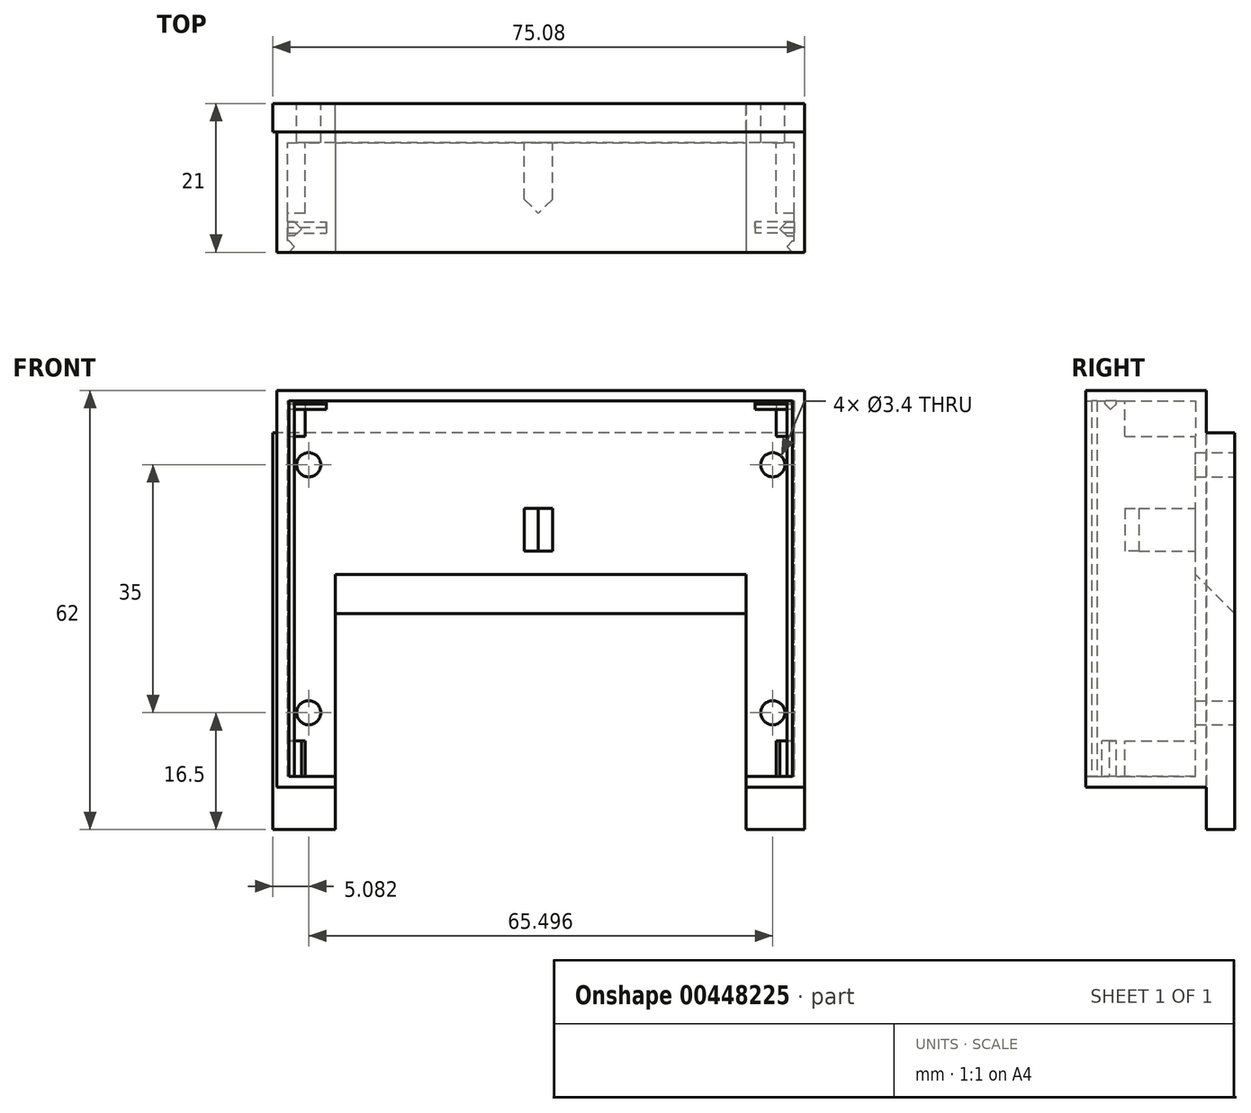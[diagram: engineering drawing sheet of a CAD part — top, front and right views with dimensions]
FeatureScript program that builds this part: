
annotation { "Feature Type Name" : "Feature", "Feature Type Description" : "" }
export const myFeature = defineFeature(function(context is Context, id is Id, definition is map)
    precondition{}
    {
        {
            var Q0;
            Q0=qCreatedBy(makeId("Front.planeOp"),FACE);
            var sketch = newSketch(context, id + "F0", { "sketchPlane" : qUnion([Q0])});
            skLineSegment(sketch, "E0.bottom", {"start": v(0, 0) * mm, "end": v(-74.5, 0) * mm});
            skLineSegment(sketch, "E0.top", {"start": v(0, 56) * mm, "end": v(-74.5, 56) * mm});
            skLineSegment(sketch, "E0.left", {"start": v(0, 0) * mm, "end": v(0, 56) * mm});
            skLineSegment(sketch, "E0.right", {"start": v(-74.5, 0) * mm, "end": v(-74.5, 56) * mm});
            skSolve(sketch);
        }
        {
            var Q0;
            Q0=makeQuery(id+"F0.imprint","IMPRINT",FACE,{"disambiguationData":[TD([[makeQuery(id+"F0.imprint","IMPRINT",EDGE,{"derivedFrom":sQuery(id+"F0.wireOp",EDGE,"E0.bottom")}),-1.0]])]});
            extrude(context, id + "F1", {"entities" : qUnion([Q0]), "depth" : 17 * mm});
        }
        {
            var Q0;
            Q0=makeQuery(id+"F1.opExtrude","CAP_FACE",FACE,{"disambiguationData":[OSD([sQuery(id+"F0.wireOp",EDGE,"E0.bottom"),sQuery(id+"F0.wireOp",EDGE,"E0.top"),sQuery(id+"F0.wireOp",EDGE,"E0.left"),sQuery(id+"F0.wireOp",EDGE,"E0.right")])],"isStart":false});
            shell(context, id + "F2", {"entities" : qUnion([Q0]), "thickness" : 1.5 * mm});
        }
        {
            var Q0;
            Q0=makeQuery(id+"F2.opShell","OFFSET_FACE",FACE,{"disambiguationData":[OSD([sQuery(id+"F0.wireOp",EDGE,"E0.bottom"),sQuery(id+"F0.wireOp",EDGE,"E0.top"),sQuery(id+"F0.wireOp",EDGE,"E0.left"),sQuery(id+"F0.wireOp",EDGE,"E0.right")])]});
            var sketch = newSketch(context, id + "F3", { "sketchPlane" : qUnion([Q0])});
            skLineSegment(sketch, "E1.bottom", {"start": v(-73, 54.5) * mm, "end": v(-70.5, 54.5) * mm});
            skLineSegment(sketch, "E1.top", {"start": v(-73, 49.5) * mm, "end": v(-70.5, 49.5) * mm});
            skLineSegment(sketch, "E1.left", {"start": v(-73, 54.5) * mm, "end": v(-73, 49.5) * mm});
            skLineSegment(sketch, "E1.right", {"start": v(-70.5, 54.5) * mm, "end": v(-70.5, 49.5) * mm});
            skLineSegment(sketch, "E2", {"start": v(-37.25, 54.5) * mm, "end": v(-37.25, 1.5) * mm, "construction": true});
            skLineSegment(sketch, "E3", {"start": v(-73, 28) * mm, "end": v(-1.5, 28) * mm, "construction": true});
            skLineSegment(sketch, "E4.MirrorCS", {"start": v(-73, 1.5) * mm, "end": v(-73, 6.5) * mm});
            skLineSegment(sketch, "E5.MirrorCS", {"start": v(-70.5, 1.5) * mm, "end": v(-70.5, 6.5) * mm});
            skLineSegment(sketch, "E6.MirrorCS", {"start": v(-73, 1.5) * mm, "end": v(-70.5, 1.5) * mm});
            skLineSegment(sketch, "E7.MirrorCS", {"start": v(-73, 6.5) * mm, "end": v(-70.5, 6.5) * mm});
            skLineSegment(sketch, "E8.MirrorCS", {"start": v(-1.5, 54.5) * mm, "end": v(-1.5, 49.5) * mm});
            skLineSegment(sketch, "E9.MirrorCS", {"start": v(-1.5, 49.5) * mm, "end": v(-4, 49.5) * mm});
            skLineSegment(sketch, "E10.MirrorCS", {"start": v(-4, 54.5) * mm, "end": v(-4, 49.5) * mm});
            skLineSegment(sketch, "E11.MirrorCS", {"start": v(-1.5, 54.5) * mm, "end": v(-4, 54.5) * mm});
            skLineSegment(sketch, "E12.MirrorCS", {"start": v(-4, 1.5) * mm, "end": v(-4, 6.5) * mm});
            skLineSegment(sketch, "E13.MirrorCS", {"start": v(-1.5, 1.5) * mm, "end": v(-1.5, 6.5) * mm});
            skLineSegment(sketch, "E14.MirrorCS", {"start": v(-1.5, 1.5) * mm, "end": v(-4, 1.5) * mm});
            skLineSegment(sketch, "E15.MirrorCS", {"start": v(-1.5, 6.5) * mm, "end": v(-4, 6.5) * mm});
            skSolve(sketch);
        }
        {
            var Q0;
            Q0=makeQuery(id+"F3.imprint","IMPRINT",FACE,{"disambiguationData":[TD([[makeQuery(id+"F3.imprint","IMPRINT",EDGE,{"derivedFrom":sQuery(id+"F3.wireOp",EDGE,"E1.bottom")}),1.0]])]});
            var Q1;
            Q1=makeQuery(id+"F3.imprint","IMPRINT",FACE,{"disambiguationData":[TD([[makeQuery(id+"F3.imprint","IMPRINT",EDGE,{"derivedFrom":sQuery(id+"F3.wireOp",EDGE,"E8.MirrorCS")}),1.0]])]});
            var Q2;
            Q2=makeQuery(id+"F3.imprint","IMPRINT",FACE,{"disambiguationData":[TD([[makeQuery(id+"F3.imprint","IMPRINT",EDGE,{"derivedFrom":sQuery(id+"F3.wireOp",EDGE,"E12.MirrorCS")}),-1.0]])]});
            var Q3;
            Q3=makeQuery(id+"F3.imprint","IMPRINT",FACE,{"disambiguationData":[TD([[makeQuery(id+"F3.imprint","IMPRINT",EDGE,{"derivedFrom":sQuery(id+"F3.wireOp",EDGE,"E4.MirrorCS")}),-1.0]])]});
            extrude(context, id + "F4", {"entities" : qUnion([Q0, Q1, Q2, Q3]), "operationType" : NewBodyOperationType.ADD, "depth" : 10 * mm});
        }
        {
            var Q0;
            Q0=makeQuery(id+"F2.opShell","OFFSET_FACE",FACE,{"disambiguationData":[OSD([sQuery(id+"F0.wireOp",EDGE,"E0.right")])]});
            var sketch = newSketch(context, id + "F5", { "sketchPlane" : qUnion([Q0])});
            skLineSegment(sketch, "E16.bottom", {"start": v(-17, 54.5) * mm, "end": v(-15.4, 54.5) * mm});
            skLineSegment(sketch, "E16.top", {"start": v(-17, -16.2) * mm, "end": v(-15.4, -16.2) * mm});
            skLineSegment(sketch, "E16.left", {"start": v(-17, 54.5) * mm, "end": v(-17, -16.2) * mm});
            skLineSegment(sketch, "E16.right", {"start": v(-15.4, 54.5) * mm, "end": v(-15.4, -16.2) * mm});
            skSolve(sketch);
        }
        {
            var Q0;
            Q0=makeQuery(id+"F2.opShell","OFFSET_FACE",FACE,{"disambiguationData":[OSD([sQuery(id+"F0.wireOp",EDGE,"E0.left")])]});
            var sketch = newSketch(context, id + "F6", { "sketchPlane" : qUnion([Q0])});
            skLineSegment(sketch, "E17.bottom", {"start": v(17, 54.5) * mm, "end": v(15.4, 54.5) * mm});
            skLineSegment(sketch, "E17.top", {"start": v(17, 1.5) * mm, "end": v(15.4, 1.5) * mm});
            skLineSegment(sketch, "E17.left", {"start": v(17, 54.5) * mm, "end": v(17, 1.5) * mm});
            skLineSegment(sketch, "E17.right", {"start": v(15.4, 54.5) * mm, "end": v(15.4, 1.5) * mm});
            skSolve(sketch);
        }
        {
            var Q0;
            Q0=makeQuery(id+"F5.imprint","IMPRINT",FACE,{"disambiguationData":[TD([[makeQuery(id+"F5.imprint","IMPRINT",EDGE,{"derivedFrom":sQuery(id+"F5.wireOp",EDGE,"E16.bottom")}),-1.0]])]});
            extrude(context, id + "F7", {"entities" : qUnion([Q0]), "operationType" : NewBodyOperationType.ADD, "depth" : 1.2 * mm, "offsetDistance" : 25 * mm});
        }
        {
            var Q0;
            Q0=makeQuery(id+"F6.imprint","IMPRINT",FACE,{"disambiguationData":[TD([[makeQuery(id+"F6.imprint","IMPRINT",EDGE,{"derivedFrom":sQuery(id+"F6.wireOp",EDGE,"E17.bottom")}),1.0]])]});
            extrude(context, id + "F8", {"entities" : qUnion([Q0]), "operationType" : NewBodyOperationType.ADD, "depth" : 1.2 * mm, "offsetDistance" : 25 * mm});
        }
        {
            var Q0;
            Q0=makeQuery(id+"F2.opShell","OFFSET_FACE",FACE,{"disambiguationData":[OSD([sQuery(id+"F0.wireOp",EDGE,"E0.top")])]});
            var sketch = newSketch(context, id + "F9", { "sketchPlane" : qUnion([Q0])});
            skLineSegment(sketch, "E18.bottom", {"start": v(-73.5, 12.7) * mm, "end": v(-67.5, 12.7) * mm});
            skLineSegment(sketch, "E18.top", {"start": v(-73.5, 14.3) * mm, "end": v(-67.5, 14.3) * mm});
            skLineSegment(sketch, "E18.left", {"start": v(-73.5, 12.7) * mm, "end": v(-73.5, 14.3) * mm});
            skLineSegment(sketch, "E18.right", {"start": v(-67.5, 12.7) * mm, "end": v(-67.5, 14.3) * mm});
            skLineSegment(sketch, "E19", {"start": v(-37.25, 17) * mm, "end": v(-37.25, 1.5) * mm, "construction": true});
            skLineSegment(sketch, "E20.MirrorCS", {"start": v(-7, 12.7) * mm, "end": v(-7, 14.3) * mm});
            skLineSegment(sketch, "E21.MirrorCS", {"start": v(-1, 12.7) * mm, "end": v(-7, 12.7) * mm});
            skLineSegment(sketch, "E22.MirrorCS", {"start": v(-1, 14.3) * mm, "end": v(-7, 14.3) * mm});
            skLineSegment(sketch, "E23.MirrorCS", {"start": v(-1, 12.7) * mm, "end": v(-1, 14.3) * mm});
            skSolve(sketch);
        }
        {
            var Q0;
            Q0=makeQuery(id+"F9.imprint","IMPRINT",FACE,{"disambiguationData":[TD([[makeQuery(id+"F9.imprint","IMPRINT",EDGE,{"derivedFrom":sQuery(id+"F9.wireOp",EDGE,"E18.bottom")}),1.0]])]});
            var Q1;
            Q1=makeQuery(id+"F9.imprint","IMPRINT",FACE,{"disambiguationData":[TD([[makeQuery(id+"F9.imprint","IMPRINT",EDGE,{"derivedFrom":sQuery(id+"F9.wireOp",EDGE,"E20.MirrorCS")}),-1.0]])]});
            extrude(context, id + "F10", {"entities" : qUnion([Q0, Q1]), "operationType" : NewBodyOperationType.ADD, "depth" : 1.2 * mm, "offsetDistance" : 25 * mm});
        }
        {
            var Q0;
            Q0=makeQuery(id+"F10.opExtrude","CAP_EDGE",EDGE,{"disambiguationData":[OSD([sQuery(id+"F9.wireOp",EDGE,"E22.MirrorCS")])],"isStart":false});
            var Q1;
            Q1=makeQuery(id+"F10.opExtrude","CAP_EDGE",EDGE,{"disambiguationData":[OSD([sQuery(id+"F9.wireOp",EDGE,"E18.top")])],"isStart":false});
            chamfer(context, id + "F11", {"entities" : qUnion([Q0, Q1]), "width" : .8 * mm, "tangentPropagation" : true});
        }
        {
            var Q0;
            Q0=makeQuery(id+"F10.opExtrude","CAP_EDGE",EDGE,{"disambiguationData":[OSD([sQuery(id+"F9.wireOp",EDGE,"E18.bottom")])],"isStart":false});
            var Q1;
            Q1=makeQuery(id+"F10.opExtrude","CAP_EDGE",EDGE,{"disambiguationData":[OSD([sQuery(id+"F9.wireOp",EDGE,"E21.MirrorCS")])],"isStart":false});
            chamfer(context, id + "F12", {"entities" : qUnion([Q0, Q1]), "chamferType" : ChamferType.TWO_OFFSETS, "width1" : .8 * mm, "oppositeDirection" : true, "width2" : .8 * mm});
        }
        {
            var Q0;
            Q0=makeQuery(id+"F2.opShell","OFFSET_FACE",FACE,{"disambiguationData":[OSD([sQuery(id+"F0.wireOp",EDGE,"E0.left")])]});
            var sketch = newSketch(context, id + "F13", { "sketchPlane" : qUnion([Q0])});
            skLineSegment(sketch, "E24.bottom", {"start": v(12.7, 1.5) * mm, "end": v(14.7, 1.5) * mm});
            skLineSegment(sketch, "E24.top", {"start": v(12.7, 6.5) * mm, "end": v(14.7, 6.5) * mm});
            skLineSegment(sketch, "E24.left", {"start": v(12.7, 1.5) * mm, "end": v(12.7, 6.5) * mm});
            skLineSegment(sketch, "E24.right", {"start": v(14.7, 1.5) * mm, "end": v(14.7, 6.5) * mm});
            skSolve(sketch);
        }
        {
            var Q0;
            Q0=makeQuery(id+"F13.imprint","IMPRINT",FACE,{"disambiguationData":[TD([[makeQuery(id+"F13.imprint","IMPRINT",EDGE,{"derivedFrom":sQuery(id+"F13.wireOp",EDGE,"E24.bottom")}),-1.0]])]});
            extrude(context, id + "F14", {"entities" : qUnion([Q0]), "operationType" : NewBodyOperationType.ADD, "depth" : 2 * mm, "offsetDistance" : 25 * mm});
        }
        {
            var Q0;
            Q0=makeQuery(id+"F2.opShell","OFFSET_FACE",FACE,{"disambiguationData":[OSD([sQuery(id+"F0.wireOp",EDGE,"E0.right")])]});
            var sketch = newSketch(context, id + "F15", { "sketchPlane" : qUnion([Q0])});
            skLineSegment(sketch, "E25.bottom", {"start": v(-12.7, 1.5) * mm, "end": v(-14.7, 1.5) * mm});
            skLineSegment(sketch, "E25.top", {"start": v(-12.7, 6.5) * mm, "end": v(-14.7, 6.5) * mm});
            skLineSegment(sketch, "E25.left", {"start": v(-12.7, 1.5) * mm, "end": v(-12.7, 6.5) * mm});
            skLineSegment(sketch, "E25.right", {"start": v(-14.7, 1.5) * mm, "end": v(-14.7, 6.5) * mm});
            skSolve(sketch);
        }
        {
            var Q0;
            Q0=makeQuery(id+"F15.imprint","IMPRINT",FACE,{"disambiguationData":[TD([[makeQuery(id+"F15.imprint","IMPRINT",EDGE,{"derivedFrom":sQuery(id+"F15.wireOp",EDGE,"E25.bottom")}),1.0]])]});
            extrude(context, id + "F16", {"entities" : qUnion([Q0]), "operationType" : NewBodyOperationType.ADD, "depth" : 2 * mm, "offsetDistance" : 25 * mm});
        }
        {
            var Q0;
            Q0=makeQuery(id+"F16.opExtrude","CAP_EDGE",EDGE,{"disambiguationData":[OSD([sQuery(id+"F15.wireOp",EDGE,"E25.right")])],"isStart":false});
            var Q1;
            Q1=makeQuery(id+"F16.opExtrude","CAP_EDGE",EDGE,{"disambiguationData":[OSD([sQuery(id+"F15.wireOp",EDGE,"E25.left")])],"isStart":false});
            var Q2;
            Q2=makeQuery(id+"F14.opExtrude","CAP_EDGE",EDGE,{"disambiguationData":[OSD([sQuery(id+"F13.wireOp",EDGE,"E24.right")])],"isStart":false});
            var Q3;
            Q3=makeQuery(id+"F14.opExtrude","CAP_EDGE",EDGE,{"disambiguationData":[OSD([sQuery(id+"F13.wireOp",EDGE,"E24.left")])],"isStart":false});
            var Q4;
            Q4=makeQuery(id+"F8.opExtrude","CAP_EDGE",EDGE,{"disambiguationData":[OSD([sQuery(id+"F6.wireOp",EDGE,"E17.left")])],"isStart":false});
            var Q5;
            Q5=makeQuery(id+"F8.opExtrude","CAP_EDGE",EDGE,{"disambiguationData":[OSD([sQuery(id+"F6.wireOp",EDGE,"E17.right")])],"isStart":false});
            var Q6;
            Q6=makeQuery(id+"F7.opExtrude","CAP_EDGE",EDGE,{"disambiguationData":[OSD([sQuery(id+"F5.wireOp",EDGE,"E16.left")])],"isStart":false});
            var Q7;
            Q7=makeQuery(id+"F7.opExtrude","CAP_EDGE",EDGE,{"disambiguationData":[OSD([sQuery(id+"F5.wireOp",EDGE,"E16.right")])],"isStart":false});
            chamfer(context, id + "F17", {"entities" : qUnion([Q0, Q1, Q2, Q3, Q4, Q5, Q6, Q7]), "width" : 1 * mm, "tangentPropagation" : true});
        }
        {
            var Q0;
            Q0=makeQuery(id+"FpiIfytRh9IFo3H_1.boolean.opBoolean","MERGE",FACE,{"derivedFrom":[makeQuery(id+"F1.opExtrude","CAP_FACE",FACE,{"disambiguationData":[OSD([sQuery(id+"F0.wireOp",EDGE,"E0.bottom"),sQuery(id+"F0.wireOp",EDGE,"E0.top"),sQuery(id+"F0.wireOp",EDGE,"E0.left"),sQuery(id+"F0.wireOp",EDGE,"E0.right")])],"isStart":true}),makeQuery(id+"FpiIfytRh9IFo3H_1.opExtrude","CAP_FACE",FACE,{"disambiguationData":[OSD([sQuery(id+"F9Pxb6aRMLhwqSh_1.wireOp",EDGE,"zlViqEuF-tvWN-PUPk-MToP-jLgJDCVNGTNb.bottom"),sQuery(id+"F9Pxb6aRMLhwqSh_1.wireOp",EDGE,"zlViqEuF-tvWN-PUPk-MToP-jLgJDCVNGTNb.top"),sQuery(id+"F9Pxb6aRMLhwqSh_1.wireOp",EDGE,"zlViqEuF-tvWN-PUPk-MToP-jLgJDCVNGTNb.left"),sQuery(id+"F9Pxb6aRMLhwqSh_1.wireOp",EDGE,"zlViqEuF-tvWN-PUPk-MToP-jLgJDCVNGTNb.right"),sQuery(id+"F9Pxb6aRMLhwqSh_1.wireOp",EDGE,"63Hq7Mwb-47zY-EonX-ODeA-Upc0aG7f1MYU"),sQuery(id+"F9Pxb6aRMLhwqSh_1.wireOp",EDGE,"4U29yTa0-IJAD-cfca-QCl1-qKSm0MAVZEq9")])],"isStart":true}),makeQuery(id+"FpiIfytRh9IFo3H_1.opExtrude","CAP_FACE",FACE,{"disambiguationData":[OSD([sQuery(id+"F9Pxb6aRMLhwqSh_1.wireOp",EDGE,"28bbedb2-4d46-419a-a5ee-67800db5490a0.MirrorCS"),sQuery(id+"F9Pxb6aRMLhwqSh_1.wireOp",EDGE,"14d362a8-6265-4b43-b875-d0e6a098b35b0.MirrorC"),sQuery(id+"F9Pxb6aRMLhwqSh_1.wireOp",EDGE,"c31abd64-f8c7-477c-a657-91555b4a46680.MirrorCS"),sQuery(id+"F9Pxb6aRMLhwqSh_1.wireOp",EDGE,"d8b9e897-c88d-44d5-8a7e-6f74603499c80.MirrorCS"),sQuery(id+"F9Pxb6aRMLhwqSh_1.wireOp",EDGE,"a43567a1-9552-4018-9fdd-2a6692d24f8d0.MirrorCS"),sQuery(id+"F9Pxb6aRMLhwqSh_1.wireOp",EDGE,"117a79f9-b130-459c-bacf-5ab90bcd88ae0.MirrorC")])],"isStart":true})]});
            var sketch = newSketch(context, id + "F18", { "sketchPlane" : qUnion([Q0])});
            skLineSegment(sketch, "E26.bottom", {"start": v(0, 50) * mm, "end": v(75.08, 50) * mm});
            skLineSegment(sketch, "E26.top", {"start": v(0, -6) * mm, "end": v(75.08, -6) * mm});
            skLineSegment(sketch, "E26.left", {"start": v(0, 50) * mm, "end": v(0, -6) * mm});
            skLineSegment(sketch, "E26.right", {"start": v(75.08, 50) * mm, "end": v(75.08, -6) * mm});
            skSolve(sketch);
        }
        {
            var Q0;
            Q0 = qSketchRegion(id + "F18", true);
            extrude(context, id + "F19", {"entities" : qUnion([Q0]), "operationType" : NewBodyOperationType.ADD, "depth" : 4 * mm, "offsetDistance" : 25 * mm});
        }
        {
            var Q0;
            {var subQ0=sQuery(id+"F18.wireOp",EDGE,"E26.right");Q0=makeQuery(id+"FpiIfytRh9IFo3H_1.boolean.opBoolean","MERGE",FACE,{"derivedFrom":[makeQuery(id+"F19.opExtrude","CAP_FACE",FACE,{"disambiguationData":[OSD([sQuery(id+"F18.wireOp",EDGE,"E26.bottom"),sQuery(id+"F18.wireOp",EDGE,"E26.top"),sQuery(id+"F18.wireOp",EDGE,"E26.left"),subQ0])],"isStart":false}),makeQuery(id+"FpiIfytRh9IFo3H_1.opExtrude","CAP_FACE",FACE,{"disambiguationData":[OSD([sQuery(id+"F9Pxb6aRMLhwqSh_1.wireOp",EDGE,"zlViqEuF-tvWN-PUPk-MToP-jLgJDCVNGTNb.bottom"),sQuery(id+"F9Pxb6aRMLhwqSh_1.wireOp",EDGE,"zlViqEuF-tvWN-PUPk-MToP-jLgJDCVNGTNb.top"),sQuery(id+"F9Pxb6aRMLhwqSh_1.wireOp",EDGE,"zlViqEuF-tvWN-PUPk-MToP-jLgJDCVNGTNb.left"),sQuery(id+"F9Pxb6aRMLhwqSh_1.wireOp",EDGE,"zlViqEuF-tvWN-PUPk-MToP-jLgJDCVNGTNb.right"),sQuery(id+"F9Pxb6aRMLhwqSh_1.wireOp",EDGE,"63Hq7Mwb-47zY-EonX-ODeA-Upc0aG7f1MYU"),sQuery(id+"F9Pxb6aRMLhwqSh_1.wireOp",EDGE,"4U29yTa0-IJAD-cfca-QCl1-qKSm0MAVZEq9")])],"isStart":true}),makeQuery(id+"FpiIfytRh9IFo3H_1.opExtrude","CAP_FACE",FACE,{"disambiguationData":[OSD([subQ0,sQuery(id+"F9Pxb6aRMLhwqSh_1.wireOp",EDGE,"28bbedb2-4d46-419a-a5ee-67800db5490a0.MirrorCS"),sQuery(id+"F9Pxb6aRMLhwqSh_1.wireOp",EDGE,"14d362a8-6265-4b43-b875-d0e6a098b35b0.MirrorC"),sQuery(id+"F9Pxb6aRMLhwqSh_1.wireOp",EDGE,"c31abd64-f8c7-477c-a657-91555b4a46680.MirrorCS"),sQuery(id+"F9Pxb6aRMLhwqSh_1.wireOp",EDGE,"a43567a1-9552-4018-9fdd-2a6692d24f8d0.MirrorCS"),sQuery(id+"F9Pxb6aRMLhwqSh_1.wireOp",EDGE,"117a79f9-b130-459c-bacf-5ab90bcd88ae0.MirrorC")])],"isStart":true})]});}
            var sketch = newSketch(context, id + "F20", { "sketchPlane" : qUnion([Q0])});
            skLineSegment(sketch, "E27.bottom", {"start": v(8.25, 24) * mm, "end": v(66.25, 24) * mm});
            skLineSegment(sketch, "E27.top", {"start": v(8.25, -6) * mm, "end": v(66.25, -6) * mm});
            skLineSegment(sketch, "E27.left", {"start": v(8.25, 24) * mm, "end": v(8.25, -6) * mm});
            skLineSegment(sketch, "E27.right", {"start": v(66.25, 24) * mm, "end": v(66.25, -6) * mm});
            skCircle(sketch, "E28", {"center": v(4.5, 10.5) * mm, "radius": 1.7 * mm});
            skCircle(sketch, "E29.MirrorC", {"center": v(4.5, 45.5) * mm, "radius": 1.7 * mm});
            skCircle(sketch, "E30.MirrorC", {"center": v(70, 10.5) * mm, "radius": 1.7 * mm});
            skCircle(sketch, "E31.MirrorC", {"center": v(70, 45.5) * mm, "radius": 1.7 * mm});
            skSolve(sketch);
        }
        {
            var Q0;
            Q0 = qSketchRegion(id + "F20", true);
            extrude(context, id + "F21", {"entities" : qUnion([Q0]), "operationType" : NewBodyOperationType.REMOVE, "oppositeDirection" : true, "depth" : 25 * mm, "offsetDistance" : 25 * mm});
        }
        {
            var Q0;
            {var subQ0=sQuery(id+"F0.wireOp",EDGE,"E0.bottom");Q0=makeQuery(id+"F21.boolean.opBoolean","SPLIT",EDGE,{"disambiguationData":[TD([makeQuery(id+"F1.opExtrude","SWEPT_FACE",FACE,{"disambiguationData":[OSD([sQuery(id+"F0.wireOp",EDGE,"E0.right")])]})])],"derivedFrom":makeQuery(id+"F1.opExtrude","CAP_EDGE",EDGE,{"disambiguationData":[OSD([subQ0])],"isStart":true})});}
            var Q1;
            {var subQ1=sQuery(id+"F0.wireOp",EDGE,"E0.bottom");Q1=makeQuery(id+"F21.boolean.opBoolean","SPLIT",EDGE,{"disambiguationData":[TD([makeQuery(id+"F1.opExtrude","SWEPT_FACE",FACE,{"disambiguationData":[OSD([sQuery(id+"F0.wireOp",EDGE,"E0.left")])]})])],"derivedFrom":makeQuery(id+"F1.opExtrude","CAP_EDGE",EDGE,{"disambiguationData":[OSD([subQ1])],"isStart":true})});}
            var Q2;
            Q2=makeQuery(id+"F21.boolean.opBoolean","INTERSECT",EDGE,{"derivedFrom":[makeQuery(id+"F2.opShell","OFFSET_FACE",FACE,{"disambiguationData":[OSD([sQuery(id+"F0.wireOp",EDGE,"E0.bottom"),sQuery(id+"F0.wireOp",EDGE,"E0.top"),sQuery(id+"F0.wireOp",EDGE,"E0.left"),sQuery(id+"F0.wireOp",EDGE,"E0.right")])]}),makeQuery(id+"F21.opExtrude","SWEPT_FACE",FACE,{"disambiguationData":[OSD([sQuery(id+"F20.wireOp",EDGE,"E27.bottom")])]})]});
            chamfer(context, id + "F22", {"entities" : qUnion([Q0, Q1, Q2]), "width" : 6 * mm, "tangentPropagation" : true});
        }
        {
            var Q0;
            {var subQ7=sQuery(id+"F3.wireOp",EDGE,"E1.top");Q0=makeQuery(id+"F3.imprint","IMPRINT",FACE,{"disambiguationData":[TD([[makeQuery(id+"F3.imprint","IMPRINT",EDGE,{"derivedFrom":subQ7}),-1.0]])]});}
            var sketch = newSketch(context, id + "F23", { "sketchPlane" : qUnion([Q0])});
            skLineSegment(sketch, "E32.bottom", {"start": v(-35.58, 33.34) * mm, "end": v(-39.58, 33.34) * mm});
            skLineSegment(sketch, "E32.top", {"start": v(-35.58, 39.34) * mm, "end": v(-39.58, 39.34) * mm});
            skLineSegment(sketch, "E32.left", {"start": v(-35.58, 33.34) * mm, "end": v(-35.58, 39.34) * mm});
            skLineSegment(sketch, "E32.right", {"start": v(-39.58, 33.34) * mm, "end": v(-39.58, 39.34) * mm});
            skPoint(sketch, "E32.middle", {"position": v(-37.58, 36.34) * mm});
            skSolve(sketch);
        }
        {
            var Q0;
            Q0 = qSketchRegion(id + "F23", true);
            extrude(context, id + "F24", {"entities" : qUnion([Q0]), "operationType" : NewBodyOperationType.ADD, "depth" : 10 * mm, "offsetDistance" : 25 * mm});
        }
        {
            var Q0;
            Q0=makeQuery(id+"F24.opExtrude","CAP_EDGE",EDGE,{"disambiguationData":[OSD([sQuery(id+"F23.wireOp",EDGE,"E32.right")])],"isStart":false});
            var Q1;
            Q1=makeQuery(id+"F24.opExtrude","CAP_EDGE",EDGE,{"disambiguationData":[OSD([sQuery(id+"F23.wireOp",EDGE,"E32.left")])],"isStart":false});
            chamfer(context, id + "F25", {"entities" : qUnion([Q0, Q1]), "width" : 2 * mm, "tangentPropagation" : true});
        }
    });
